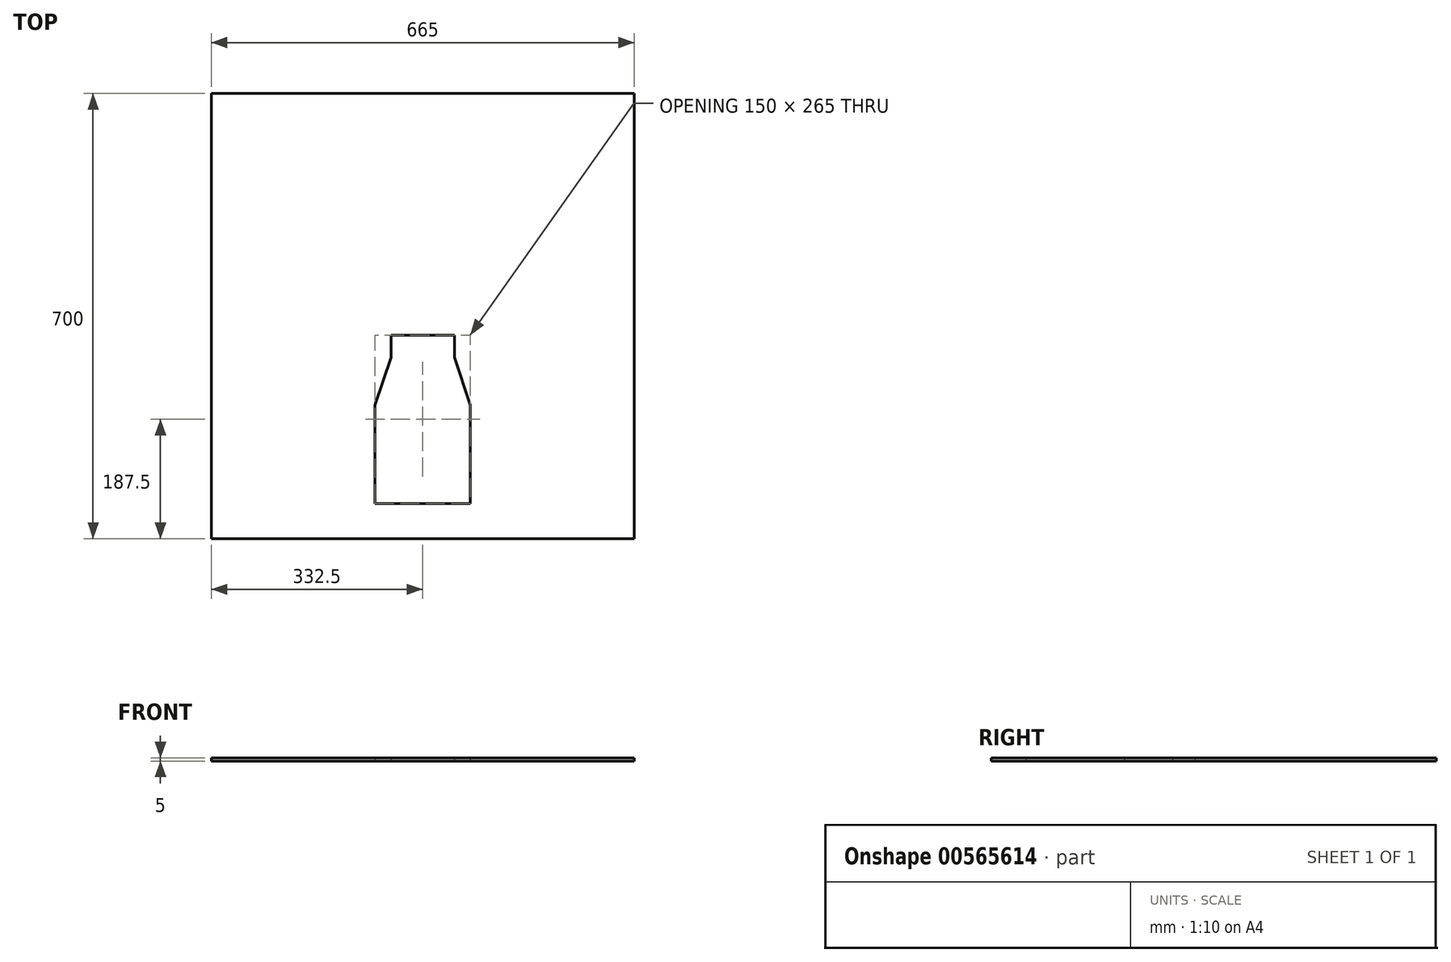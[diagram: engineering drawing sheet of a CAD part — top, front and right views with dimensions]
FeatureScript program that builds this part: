
annotation { "Feature Type Name" : "Feature", "Feature Type Description" : "" }
export const myFeature = defineFeature(function(context is Context, id is Id, definition is map)
    precondition{}
    {
        {
            var Q0;
            Q0=qCreatedBy(makeId("Top.planeOp"),FACE);
            var sketch = newSketch(context, id + "F0", { "sketchPlane" : qUnion([Q0])});
            skLineSegment(sketch, "E0.bottom", {"start": v(-332.5, 350) * mm, "end": v(332.5, 350) * mm});
            skLineSegment(sketch, "E0.top", {"start": v(-332.5, -350) * mm, "end": v(332.5, -350) * mm});
            skLineSegment(sketch, "E0.left", {"start": v(-332.5, 350) * mm, "end": v(-332.5, -350) * mm});
            skLineSegment(sketch, "E0.right", {"start": v(332.5, 350) * mm, "end": v(332.5, -350) * mm});
            skLineSegment(sketch, "E1.bottom", {"start": v(50, -30) * mm, "end": v(-50, -30) * mm});
            skLineSegment(sketch, "E1.left", {"start": v(50, -30) * mm, "end": v(50, -65) * mm});
            skLineSegment(sketch, "E1.right", {"start": v(-50, -30) * mm, "end": v(-50, -65) * mm});
            skLineSegment(sketch, "E2.top", {"start": v(-75, -295) * mm, "end": v(75, -295) * mm});
            skLineSegment(sketch, "E2.left", {"start": v(-75, -140) * mm, "end": v(-75, -295) * mm});
            skLineSegment(sketch, "E2.right", {"start": v(75, -140) * mm, "end": v(75, -295) * mm});
            skLineSegment(sketch, "E3", {"start": v(50, -65) * mm, "end": v(75, -140) * mm});
            skLineSegment(sketch, "E4", {"start": v(-50, -65) * mm, "end": v(-75, -140) * mm});
            skSolve(sketch);
        }
        {
            var Q0;
            Q0 = qSketchRegion(id + "F0", true);
            extrude(context, id + "F1", {"entities" : qUnion([Q0]), "depth" : 5 * mm, "offsetDistance" : 25 * mm});
        }
    });
